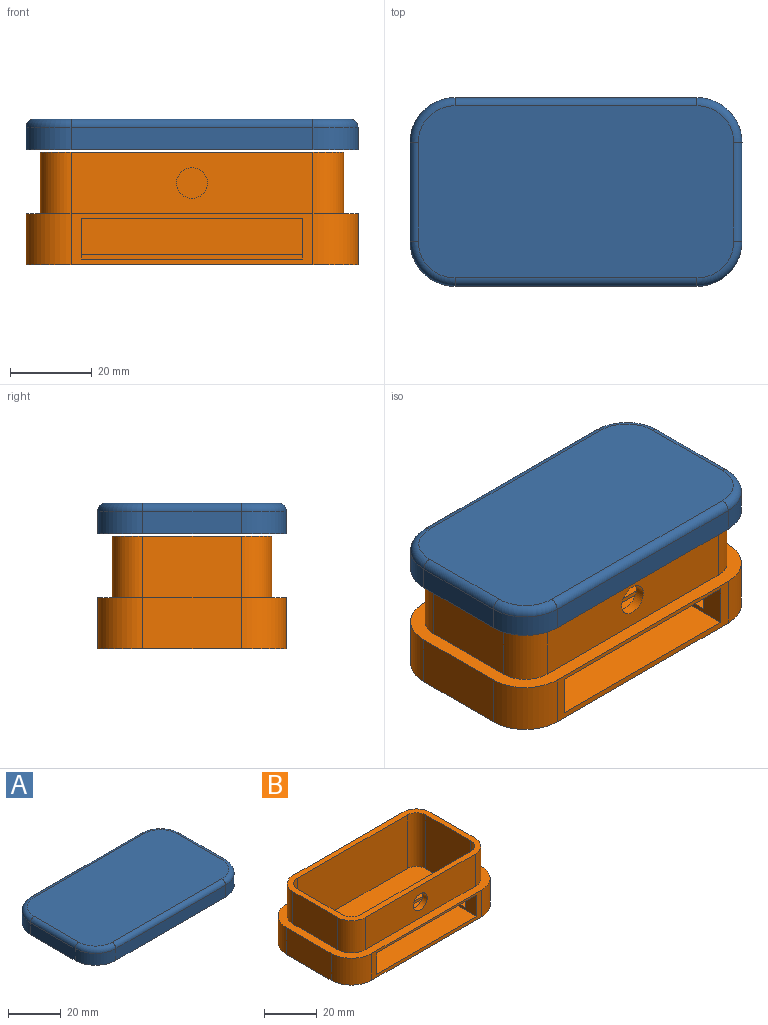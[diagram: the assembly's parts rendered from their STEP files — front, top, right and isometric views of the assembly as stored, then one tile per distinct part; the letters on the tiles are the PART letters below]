
ASSEMBLY  parts=2 mates=1
PART A: 27 faces, bbox 82.8x47.8x7.5 mm
  f0: cylinder r=11mm len=11mm, axis (0,0,1), area 95mm2, adj f1,f15,f16,f21
  f1: plane 24x5.5mm, normal (-1,0,0), area 132mm2, adj f0,f2,f16,f19
  f2: cylinder r=11mm len=11mm, axis (0,0,1), area 95mm2, adj f1,f3,f16,f20
  f3: plane 59x5.5mm, normal (0,-1,0), area 324.5mm2, adj f2,f4,f16,f22
  f4: cylinder r=11mm len=11mm, axis (0,0,1), area 95mm2, adj f3,f5,f16,f24
  f5: plane 24x5.5mm, normal (1,0,0), area 132mm2, adj f4,f6,f16,f26
  f6: cylinder r=11mm len=11mm, axis (0,0,1), area 95mm2, adj f5,f15,f16,f25
  f7: plane 59x5mm, normal (0,1,0), area 295mm2, adj f8,f14,f16,f17
  f8: cylinder r=9mm len=9mm, axis (0,0,1), area 70.7mm2, adj f7,f9,f16,f17
  f9: plane 24x5mm, normal (1,0,0), area 120mm2, adj f8,f10,f16,f17
  f10: cylinder r=9mm len=9mm, axis (0,0,1), area 70.7mm2, adj f9,f11,f16,f17
  f11: plane 59x5mm, normal (0,-1,0), area 295mm2, adj f10,f12,f16,f17
  f12: cylinder r=9mm len=9mm, axis (0,0,1), area 70.7mm2, adj f11,f13,f16,f17
  f13: plane 24x5mm, normal (-1,0,0), area 120mm2, adj f12,f14,f16,f17
  f14: cylinder r=9mm len=9mm, axis (0,0,1), area 70.7mm2, adj f7,f13,f16,f17
  f15: plane 59x5.5mm, normal (0,1,0), area 324.5mm2, adj f0,f6,f16,f23
  f16: plane 81x46mm, normal (0,0,-1), area 457.7mm2, adj f0,f1,f2,f3,f4,f5,f6,f7
  f17: plane 77x42mm, normal (0,0,-1), area 3164.5mm2, adj f7,f8,f9,f10,f11,f12,f13,f14
  f18: plane 77x42mm, normal (0,0,1), area 3164.5mm2, adj f19,f20,f21,f22,f23,f24,f25,f26
  f19: cylinder r=2mm len=24mm, axis (0,-1,0), area 75.4mm2, adj f1,f18,f20,f21
  f20: torus R=9mm, axis (0,0,1), area 50.7mm2, adj f2,f18,f19,f22
  f21: torus R=9mm, axis (0,0,1), area 50.7mm2, adj f0,f18,f19,f23
  f22: cylinder r=2mm len=59mm, axis (1,0,0), area 185.4mm2, adj f3,f18,f20,f24
  f23: cylinder r=2mm len=59mm, axis (-1,0,0), area 185.4mm2, adj f15,f18,f21,f25
  f24: torus R=9mm, axis (0,0,1), area 50.7mm2, adj f4,f18,f22,f26
  f25: torus R=9mm, axis (0,0,1), area 50.7mm2, adj f6,f18,f23,f26
  f26: cylinder r=2mm len=24mm, axis (0,1,0), area 75.4mm2, adj f5,f18,f24,f25
PART B: 34 faces, bbox 81x46x27.5 mm
  f0: plane 59x25mm, normal (0,1,0), area 947.4mm2, adj f1,f19,f25,f26,f29,f30,f31,f33
  f1: plane 69x34mm, normal (0,0,1), area 1406.5mm2, adj f0,f19,f20,f21,f22,f23,f24,f25
  f2: cylinder r=11mm len=12.5mm, axis (0,0,-1), area 216mm2, adj f3,f9,f10,f27
  f3: plane 59x12.5mm, normal (0,-1,0), area 197.5mm2, adj f2,f4,f10,f27,f28,f29,f30,f31
  f4: cylinder r=11mm len=12.5mm, axis (0,0,-1), area 216mm2, adj f3,f5,f10,f27
  f5: plane 24x12.5mm, normal (1,0,0), area 300mm2, adj f4,f6,f10,f27
  f6: cylinder r=11mm len=12.5mm, axis (0,0,-1), area 216mm2, adj f5,f7,f10,f27
  f7: plane 59x12.5mm, normal (0,1,0), area 737.5mm2, adj f6,f8,f10,f27
  f8: cylinder r=11mm len=12.5mm, axis (0,0,-1), area 216mm2, adj f7,f9,f10,f27
  f9: plane 24x12.5mm, normal (-1,0,0), area 300mm2, adj f2,f8,f10,f27
  f10: plane 81x46mm, normal (0,0,1), area 784.4mm2, adj f2,f3,f4,f5,f6,f7,f8,f9
  f11: plane 24x15mm, normal (-1,0,0), area 360mm2, adj f10,f15,f16,f26
  f12: plane 59x15mm, normal (0,1,0), area 885mm2, adj f10,f15,f18,f26
  f13: plane 24x15mm, normal (1,0,0), area 360mm2, adj f10,f17,f18,f26
  f14: plane 59x15mm, normal (0,-1,0), area 840.8mm2, adj f10,f16,f17,f26,f33
  f15: cylinder r=7.5mm len=15mm, axis (0,0,-1), area 176.7mm2, adj f10,f11,f12,f26
  f16: cylinder r=7.5mm len=15mm, axis (0,0,-1), area 176.7mm2, adj f10,f11,f14,f26
  f17: cylinder r=7.5mm len=15mm, axis (0,0,-1), area 176.7mm2, adj f10,f13,f14,f26
  f18: cylinder r=7.5mm len=15mm, axis (0,0,-1), area 176.7mm2, adj f10,f12,f13,f26
  f19: cylinder r=5mm len=25mm, axis (0,0,-1), area 196.3mm2, adj f0,f1,f20,f26
  f20: plane 25x24mm, normal (1,0,0), area 600mm2, adj f1,f19,f21,f26
  f21: cylinder r=5mm len=25mm, axis (0,0,-1), area 196.3mm2, adj f1,f20,f22,f26
  f22: plane 59x25mm, normal (0,-1,0), area 1475mm2, adj f1,f21,f23,f26
  f23: cylinder r=5mm len=25mm, axis (0,0,-1), area 196.3mm2, adj f1,f22,f24,f26
  f24: plane 25x24mm, normal (-1,0,0), area 600mm2, adj f1,f23,f25,f26
  f25: cylinder r=5mm len=25mm, axis (0,0,-1), area 196.3mm2, adj f0,f1,f24,f26
  f26: plane 74x39mm, normal (0,0,1), area 513.2mm2, adj f0,f11,f12,f13,f14,f15,f16,f17
  f27: plane 81x46mm, normal (0,0,-1), area 3622.1mm2, adj f2,f3,f4,f5,f6,f7,f8,f9
  f28: plane 54x23mm, normal (0,0,1), area 1242mm2, adj f3,f30,f31,f32
  f29: plane 54x6mm, normal (0,0,-1), area 324mm2, adj f0,f3,f30,f31
  f30: plane 23x10mm, normal (1,0,0), area 77.8mm2, adj f0,f1,f3,f28,f29,f32
  f31: plane 23x10mm, normal (-1,0,0), area 77.8mm2, adj f0,f1,f3,f28,f29,f32
  f32: plane 54x1.05mm, normal (0,-1,0), area 56.6mm2, adj f1,f28,f30,f31
  f33: cylinder r=3.75mm len=7.5mm, axis (0,1,0), area 58.9mm2, adj f0,f14
PLACE A t=(-46.72,2.28,5.17)mm
PLACE B t=(-46.72,2.28,-5.43)mm
MATE slider A.f17 <-> B.f26  axis (0,0,-1) through (-46.72,2.28,25.17)mm
